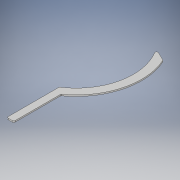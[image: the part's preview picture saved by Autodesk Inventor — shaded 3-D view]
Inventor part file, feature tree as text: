
AUTODESK INVENTOR PART (.ipt)
format: ipt  version: 2017 (Build 210142000, 142)  size: 124,416 bytes
history: native  units: in
note: dims shown in document units (in); Inventor stores cm internally (conversion verified against a paired STEP export)
features: extrude x1, sketch x1
ambient origin geometry x8: Origin, YZ Plane, XZ Plane, XY Plane, X Axis, Y Axis, Z Axis, Center Point
bodies: Solid1 (feature_tree)
feature tree (2):
  extrude  "Extrusion1"  Depth=0.125in
  sketch  "Sketch1"  dims[d1=5.2in d2=0.2272in d3=0.5978in d4=11.9in d5=1.152in d6=4.75in d8=0.125in d9=0.125in d10=0.125in d11=0.125in d12=0.0in]
